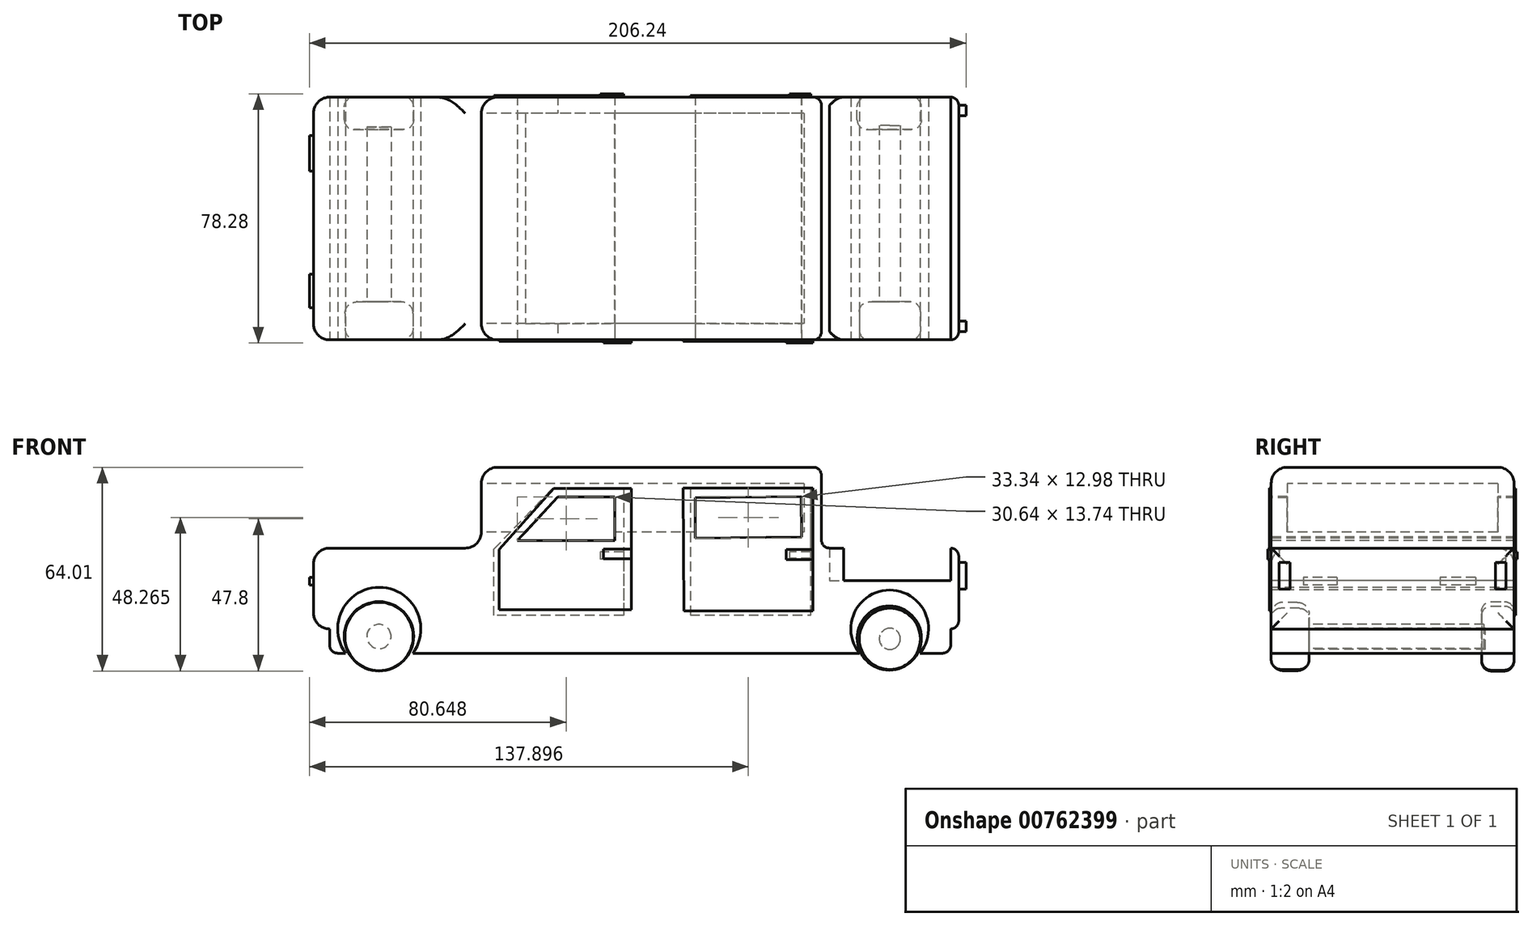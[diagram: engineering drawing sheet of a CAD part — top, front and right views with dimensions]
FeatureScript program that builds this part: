
annotation { "Feature Type Name" : "Feature", "Feature Type Description" : "" }
export const myFeature = defineFeature(function(context is Context, id is Id, definition is map)
    precondition{}
    {
        {
            var Q0;
            Q0=qCreatedBy(makeId("Top.planeOp"),FACE);
            var sketch = newSketch(context, id + "F0", { "sketchPlane" : qUnion([Q0])});
            skLineSegment(sketch, "E0.bottom", {"start": v(-103.87, 60.83) * mm, "end": v(98.81, 60.83) * mm});
            skLineSegment(sketch, "E0.top", {"start": v(-103.87, -15.43) * mm, "end": v(98.81, -15.43) * mm});
            skLineSegment(sketch, "E0.left", {"start": v(-103.87, 60.83) * mm, "end": v(-103.87, -15.43) * mm});
            skLineSegment(sketch, "E0.right", {"start": v(98.81, 60.83) * mm, "end": v(98.81, -15.43) * mm});
            skSolve(sketch);
        }
        {
            var Q0;
            Q0 = qSketchRegion(id + "F0", true);
            extrude(context, id + "F1", {"entities" : qUnion([Q0]), "depth" : 25.4 * mm, "offsetDistance" : 25.4 * mm});
        }
        {
            var Q0;
            Q0=makeQuery(id+"F1.opExtrude","CAP_FACE",FACE,{"disambiguationData":[OSD([sQuery(id+"F0.wireOp",EDGE,"E0.bottom"),sQuery(id+"F0.wireOp",EDGE,"E0.top"),sQuery(id+"F0.wireOp",EDGE,"E0.left"),sQuery(id+"F0.wireOp",EDGE,"E0.right")])],"isStart":false});
            var sketch = newSketch(context, id + "F2", { "sketchPlane" : qUnion([Q0])});
            skLineSegment(sketch, "E1.bottom", {"start": v(-51.1, 60.83) * mm, "end": v(55.69, 60.83) * mm});
            skLineSegment(sketch, "E1.top", {"start": v(-51.1, -15.43) * mm, "end": v(55.69, -15.43) * mm});
            skLineSegment(sketch, "E1.left", {"start": v(-51.1, 60.83) * mm, "end": v(-51.1, -15.43) * mm});
            skLineSegment(sketch, "E1.right", {"start": v(55.69, 60.83) * mm, "end": v(55.69, -15.43) * mm});
            skSolve(sketch);
        }
        {
            var Q0;
            Q0 = qSketchRegion(id + "F2", true);
            extrude(context, id + "F3", {"entities" : qUnion([Q0]), "operationType" : NewBodyOperationType.ADD, "depth" : 25.4 * mm, "offsetDistance" : 25.4 * mm});
        }
        {
            var Q0;
            Q0=makeQuery(id+"F3.opExtrude","CAP_EDGE",EDGE,{"disambiguationData":[OSD([sQuery(id+"F2.wireOp",EDGE,"E1.left")])],"isStart":false});
            var Q1;
            Q1=makeQuery(id+"F3.opExtrude","SWEPT_FACE",FACE,{"disambiguationData":[OSD([sQuery(id+"F2.wireOp",EDGE,"E1.left")])]});
            var Q2;
            Q2=makeQuery(id+"F1.opExtrude","CAP_EDGE",EDGE,{"disambiguationData":[OSD([sQuery(id+"F0.wireOp",EDGE,"E0.left")])],"isStart":false});
            var Q3;
            Q3=makeQuery(id+"F1.opExtrude","SWEPT_FACE",FACE,{"disambiguationData":[OSD([sQuery(id+"F0.wireOp",EDGE,"E0.left")])]});
            fillet(context, id + "F4", {"entities" : qUnion([Q0, Q1, Q2, Q3]), "radius" : 5.08 * mm, "tangentPropagation" : true, "allowEdgeOverflow" : false});
        }
        {
            var Q0;
            Q0=makeQuery(id+"F3.opExtrude","CAP_EDGE",EDGE,{"disambiguationData":[OSD([sQuery(id+"F2.wireOp",EDGE,"E1.right")])],"isStart":false});
            var Q1;
            Q1=makeQuery(id+"F3.opExtrude","SWEPT_FACE",FACE,{"disambiguationData":[OSD([sQuery(id+"F2.wireOp",EDGE,"E1.right")])]});
            fillet(context, id + "F5", {"entities" : qUnion([Q0, Q1]), "radius" : 2.54 * mm, "tangentPropagation" : true, "allowEdgeOverflow" : false});
        }
        {
            var Q0;
            Q0=makeQuery(id+"F1.opExtrude","SWEPT_EDGE",EDGE,{"disambiguationData":[OSD([sQuery(id+"F0.wireOp",EDGE,"E0.bottom"),sQuery(id+"F0.wireOp",EDGE,"E0.right")])]});
            var Q1;
            Q1=makeQuery(id+"F1.opExtrude","SWEPT_FACE",FACE,{"disambiguationData":[OSD([sQuery(id+"F0.wireOp",EDGE,"E0.right")])]});
            fillet(context, id + "F6", {"entities" : qUnion([Q0, Q1]), "radius" : 2.54 * mm, "tangentPropagation" : true, "allowEdgeOverflow" : false});
        }
        {
            var Q0;
            Q0=makeQuery(id+"F1.opExtrude","CAP_FACE",FACE,{"disambiguationData":[OSD([sQuery(id+"F0.wireOp",EDGE,"E0.bottom"),sQuery(id+"F0.wireOp",EDGE,"E0.top"),sQuery(id+"F0.wireOp",EDGE,"E0.left"),sQuery(id+"F0.wireOp",EDGE,"E0.right")])],"isStart":true});
            var sketch = newSketch(context, id + "F7", { "sketchPlane" : qUnion([Q0])});
            skLineSegment(sketch, "E2.bottom", {"start": v(-98.79, 15.43) * mm, "end": v(96.27, 15.43) * mm});
            skLineSegment(sketch, "E2.top", {"start": v(-98.79, -60.83) * mm, "end": v(96.27, -60.83) * mm});
            skLineSegment(sketch, "E2.left", {"start": v(-98.79, 15.43) * mm, "end": v(-98.79, -60.83) * mm});
            skLineSegment(sketch, "E2.right", {"start": v(96.27, 15.43) * mm, "end": v(96.27, -60.83) * mm});
            skSolve(sketch);
        }
        {
            var Q0;
            Q0 = qSketchRegion(id + "F7", true);
            extrude(context, id + "F8", {"entities" : qUnion([Q0]), "operationType" : NewBodyOperationType.ADD, "depth" : 7.62 * mm, "offsetDistance" : 25.4 * mm});
        }
        {
            var Q0;
            Q0=makeQuery(id+"F8.opExtrude","CAP_EDGE",EDGE,{"disambiguationData":[OSD([sQuery(id+"F7.wireOp",EDGE,"E2.left")])],"isStart":false});
            var Q1;
            {var subQ0=sQuery(id+"F0.wireOp",EDGE,"E0.left");Q1=makeQuery(id+"F4.opFillet","BLEND_EDGE",EDGE,{"blendedFrom":[makeQuery(id+"F1.opExtrude","CAP_EDGE",EDGE,{"disambiguationData":[OSD([subQ0])],"isStart":true}),makeQuery(id+"F1.opExtrude","SWEPT_FACE",FACE,{"disambiguationData":[OSD([subQ0])]})],"blendedInto":[makeQuery(id+"F1.opExtrude","SWEPT_FACE",FACE,{"disambiguationData":[OSD([subQ0])]})]});}
            var Q2;
            Q2=makeQuery(id+"F8.opExtrude","CAP_EDGE",EDGE,{"disambiguationData":[OSD([sQuery(id+"F7.wireOp",EDGE,"E2.right")])],"isStart":false});
            fillet(context, id + "F9", {"entities" : qUnion([Q0, Q1, Q2]), "radius" : 2.54 * mm, "tangentPropagation" : true, "allowEdgeOverflow" : false});
        }
        {
            var Q0;
            Q0=makeQuery(id+"F8.boolean.opBoolean","MERGE",FACE,{"derivedFrom":[makeQuery(id+"F3.boolean.opBoolean","MERGE",FACE,{"derivedFrom":[makeQuery(id+"F1.opExtrude","SWEPT_FACE",FACE,{"disambiguationData":[OSD([sQuery(id+"F0.wireOp",EDGE,"E0.bottom")])]}),makeQuery(id+"F3.opExtrude","SWEPT_FACE",FACE,{"disambiguationData":[OSD([sQuery(id+"F2.wireOp",EDGE,"E1.bottom")])]})]}),makeQuery(id+"F8.opExtrude","SWEPT_FACE",FACE,{"disambiguationData":[OSD([sQuery(id+"F7.wireOp",EDGE,"E2.top")])]})]});
            var sketch = newSketch(context, id + "F10", { "sketchPlane" : qUnion([Q0])});
            skLineSegment(sketch, "E3", {"start": v(-54.63, 24.35) * mm, "end": v(48.07, 24.35) * mm});
            skSolve(sketch);
        }
        {
            var Q0;
            Q0=makeQuery(id+"F3.opExtrude","CAP_EDGE",EDGE,{"disambiguationData":[OSD([sQuery(id+"F2.wireOp",EDGE,"E1.bottom")])],"isStart":false});
            var Q1;
            Q1=makeQuery(id+"F3.opExtrude","CAP_EDGE",EDGE,{"disambiguationData":[OSD([sQuery(id+"F2.wireOp",EDGE,"E1.top")])],"isStart":false});
            fillet(context, id + "F11", {"entities" : qUnion([Q0, Q1]), "radius" : 5.08 * mm, "tangentPropagation" : true, "allowEdgeOverflow" : false});
        }
        {
            var Q0;
            Q0=makeQuery(id+"F8.boolean.opBoolean","MERGE",FACE,{"derivedFrom":[makeQuery(id+"F3.boolean.opBoolean","MERGE",FACE,{"derivedFrom":[makeQuery(id+"F1.opExtrude","SWEPT_FACE",FACE,{"disambiguationData":[OSD([sQuery(id+"F0.wireOp",EDGE,"E0.top")])]}),makeQuery(id+"F3.opExtrude","SWEPT_FACE",FACE,{"disambiguationData":[OSD([sQuery(id+"F2.wireOp",EDGE,"E1.top")])]})]}),makeQuery(id+"F8.opExtrude","SWEPT_FACE",FACE,{"disambiguationData":[OSD([sQuery(id+"F7.wireOp",EDGE,"E2.bottom")])]})]});
            var sketch = newSketch(context, id + "F12", { "sketchPlane" : qUnion([Q0])});
            skLineSegment(sketch, "E4", {"start": v(-47.73, 24.83) * mm, "end": v(53.15, 24.83) * mm});
            skLineSegment(sketch, "E5", {"start": v(53.15, 24.83) * mm, "end": v(29.7, 24.83) * mm});
            skLineSegment(sketch, "E6", {"start": v(29.7, 24.83) * mm, "end": v(29.7, 45.72) * mm});
            skSolve(sketch);
        }
        {
            var Q0;
            {var subQ15=sQuery(id+"F12.wireOp",EDGE,"E4");Q0=makeQuery(id+"F12.imprint","IMPRINT",FACE,{"disambiguationData":[TD([[makeQuery(id+"F12.imprint","IMPRINT",EDGE,{"derivedFrom":subQ15}),-1.0]])]});}
            var sketch = newSketch(context, id + "F13", { "sketchPlane" : qUnion([Q0])});
            skCircle(sketch, "E7", {"center": v(-83.66, 0) * mm, "radius": 11.07 * mm});
            skCircle(sketch, "E8", {"center": v(76.6, 0) * mm, "radius": 11.02 * mm});
            skSolve(sketch);
        }
        {
            var Q0;
            Q0=makeQuery(id+"F1.opExtrude","SWEPT_FACE",FACE,{"disambiguationData":[OSD([sQuery(id+"F0.wireOp",EDGE,"E0.left")])]});
            var sketch = newSketch(context, id + "F14", { "sketchPlane" : qUnion([Q0])});
            skSolve(sketch);
        }
        {
            var Q0;
            {var subQ0=sQuery(id+"F0.wireOp",EDGE,"E0.top");var subQ1=sQuery(id+"F0.wireOp",EDGE,"E0.right");var subQ2=sQuery(id+"F0.wireOp",EDGE,"E0.bottom");Q0=makeQuery(id+"F3.boolean.opBoolean","SPLIT",FACE,{"disambiguationData":[TD([makeQuery(id+"F1.opExtrude","SWEPT_FACE",FACE,{"disambiguationData":[OSD([subQ1])]})])],"derivedFrom":makeQuery(id+"F1.opExtrude","CAP_FACE",FACE,{"disambiguationData":[OSD([subQ2,subQ0,sQuery(id+"F0.wireOp",EDGE,"E0.left"),subQ1])],"isStart":false})});}
            var sketch = newSketch(context, id + "F15", { "sketchPlane" : qUnion([Q0])});
            skSolve(sketch);
        }
        {
            var Q0;
            Q0 = qSketchRegion(id + "F13", true);
            extrude(context, id + "F16", {"entities" : qUnion([Q0]), "operationType" : NewBodyOperationType.REMOVE, "oppositeDirection" : true, "depth" : 78.74 * mm, "offsetDistance" : 25.4 * mm});
        }
        {
            var Q0;
            {var subQ1=sQuery(id+"F0.wireOp",EDGE,"E0.top");var subQ3=sQuery(id+"F0.wireOp",EDGE,"E0.right");var subQ4=makeQuery(id+"F1.opExtrude","SWEPT_FACE",FACE,{"disambiguationData":[OSD([subQ3])]});var subQ5=sQuery(id+"F0.wireOp",EDGE,"E0.bottom");var subQ8=sQuery(id+"F2.wireOp",EDGE,"E1.right");var subQ10=makeQuery(id+"F1.opExtrude","CAP_FACE",FACE,{"disambiguationData":[OSD([subQ5,subQ1,sQuery(id+"F0.wireOp",EDGE,"E0.left"),subQ3])],"isStart":false});var subQ11=makeQuery(id+"F3.boolean.opBoolean","SPLIT",FACE,{"disambiguationData":[TD([subQ4])],"derivedFrom":subQ10});Q0=makeQuery(id+"F15.imprint","IMPRINT",FACE,{"disambiguationData":[TD([[makeQuery(id+"F15.imprint","IMPRINT",EDGE,{"derivedFrom":makeQuery(id+"F5.opFillet","BLEND_EDGE",EDGE,{"blendedFrom":[makeQuery(id+"F3.opExtrude","CAP_EDGE",EDGE,{"disambiguationData":[OSD([subQ8])],"isStart":true}),subQ11],"blendedInto":[subQ11]})}),1.0]])]});}
            extrude(context, id + "F17", {"entities" : qUnion([Q0]), "operationType" : NewBodyOperationType.REMOVE, "oppositeDirection" : true, "depth" : 10.16 * mm, "offsetDistance" : 25.4 * mm});
        }
        {
            var Q0;
            {var subQ15=sQuery(id+"F12.wireOp",EDGE,"E4");Q0=makeQuery(id+"F12.imprint","IMPRINT",FACE,{"disambiguationData":[TD([[makeQuery(id+"F12.imprint","IMPRINT",EDGE,{"derivedFrom":subQ15}),-1.0]])]});}
            var sketch = newSketch(context, id + "F18", { "sketchPlane" : qUnion([Q0])});
            skLineSegment(sketch, "E9", {"start": v(12.54, 5.62) * mm, "end": v(53.01, 5.62) * mm});
            skLineSegment(sketch, "E10", {"start": v(53.01, 5.62) * mm, "end": v(53.01, 44.28) * mm});
            skLineSegment(sketch, "E11", {"start": v(53.01, 44.28) * mm, "end": v(12.23, 44.28) * mm});
            skLineSegment(sketch, "E12", {"start": v(12.23, 44.28) * mm, "end": v(12.54, 5.62) * mm});
            skLineSegment(sketch, "E13.bottom", {"start": v(53.01, 24.95) * mm, "end": v(46.24, 24.95) * mm});
            skLineSegment(sketch, "E13.top", {"start": v(53.01, 22.79) * mm, "end": v(46.24, 22.79) * mm});
            skLineSegment(sketch, "E13.left", {"start": v(53.01, 24.95) * mm, "end": v(53.01, 22.79) * mm});
            skLineSegment(sketch, "E13.right", {"start": v(46.24, 24.95) * mm, "end": v(46.24, 22.79) * mm});
            skSolve(sketch);
        }
        {
            var Q0;
            Q0 = qSketchRegion(id + "F18", true);
            extrude(context, id + "F19", {"entities" : qUnion([Q0]), "operationType" : NewBodyOperationType.ADD, "depth" : 0.5 * mm, "offsetDistance" : 25.4 * mm});
        }
        {
            var Q0;
            {var subQ7=sQuery(id+"F10.wireOp",EDGE,"E3");Q0=makeQuery(id+"F10.imprint","IMPRINT",FACE,{"disambiguationData":[TD([[makeQuery(id+"F10.imprint","IMPRINT",EDGE,{"derivedFrom":subQ7}),1.0]])]});}
            var sketch = newSketch(context, id + "F20", { "sketchPlane" : qUnion([Q0])});
            skLineSegment(sketch, "E14", {"start": v(47.15, 25.07) * mm, "end": v(28.86, 44.1) * mm});
            skLineSegment(sketch, "E15", {"start": v(28.86, 44.1) * mm, "end": v(6.43, 44.1) * mm});
            skLineSegment(sketch, "E16", {"start": v(6.43, 44.1) * mm, "end": v(6.43, 4.2) * mm});
            skLineSegment(sketch, "E17", {"start": v(6.43, 4.2) * mm, "end": v(47.15, 4.2) * mm});
            skLineSegment(sketch, "E18", {"start": v(47.15, 4.2) * mm, "end": v(47.15, 25.07) * mm});
            skLineSegment(sketch, "E19", {"start": v(-14.5, 44.1) * mm, "end": v(-14.5, 4.4) * mm});
            skLineSegment(sketch, "E20", {"start": v(-14.5, 4.4) * mm, "end": v(-52.38, 4.4) * mm});
            skLineSegment(sketch, "E21", {"start": v(-52.38, 4.4) * mm, "end": v(-52.38, 44.1) * mm});
            skLineSegment(sketch, "E22", {"start": v(-52.38, 44.1) * mm, "end": v(-14.5, 44.1) * mm});
            skLineSegment(sketch, "E23.bottom", {"start": v(-52.38, 24.24) * mm, "end": v(-46.53, 24.24) * mm});
            skLineSegment(sketch, "E23.top", {"start": v(-52.38, 26.16) * mm, "end": v(-46.53, 26.16) * mm});
            skLineSegment(sketch, "E23.left", {"start": v(-52.38, 24.24) * mm, "end": v(-52.38, 26.16) * mm});
            skLineSegment(sketch, "E23.right", {"start": v(-46.53, 24.24) * mm, "end": v(-46.53, 26.16) * mm});
            skLineSegment(sketch, "E24.bottom", {"start": v(6.43, 24.15) * mm, "end": v(15.68, 24.15) * mm});
            skLineSegment(sketch, "E24.top", {"start": v(6.43, 26.16) * mm, "end": v(15.68, 26.16) * mm});
            skLineSegment(sketch, "E24.left", {"start": v(6.43, 24.15) * mm, "end": v(6.43, 26.16) * mm});
            skLineSegment(sketch, "E24.right", {"start": v(15.68, 24.15) * mm, "end": v(15.68, 26.16) * mm});
            skSolve(sketch);
        }
        {
            var Q0;
            Q0 = qSketchRegion(id + "F20", true);
            extrude(context, id + "F21", {"entities" : qUnion([Q0]), "operationType" : NewBodyOperationType.ADD, "depth" : 0.5 * mm, "offsetDistance" : 25.4 * mm});
        }
        {
            var Q0;
            Q0=makeQuery(id+"F21.opExtrude","CAP_FACE",FACE,{"disambiguationData":[OSD([sQuery(id+"F20.wireOp",EDGE,"E14"),sQuery(id+"F20.wireOp",EDGE,"E15"),sQuery(id+"F20.wireOp",EDGE,"E16"),sQuery(id+"F20.wireOp",EDGE,"E17"),sQuery(id+"F20.wireOp",EDGE,"E18"),sQuery(id+"F20.wireOp",EDGE,"E24.left")])],"isStart":false});
            var sketch = newSketch(context, id + "F22", { "sketchPlane" : qUnion([Q0])});
            skLineSegment(sketch, "E25.bottom", {"start": v(6.43, 24.15) * mm, "end": v(13.75, 24.15) * mm});
            skLineSegment(sketch, "E25.top", {"start": v(6.43, 21.96) * mm, "end": v(13.75, 21.96) * mm});
            skLineSegment(sketch, "E25.left", {"start": v(6.43, 24.15) * mm, "end": v(6.43, 21.96) * mm});
            skLineSegment(sketch, "E25.right", {"start": v(13.75, 24.15) * mm, "end": v(13.75, 21.96) * mm});
            skSolve(sketch);
        }
        {
            var Q0;
            Q0 = qSketchRegion(id + "F22", true);
            extrude(context, id + "F23", {"entities" : qUnion([Q0]), "operationType" : NewBodyOperationType.ADD, "depth" : 0.5 * mm, "offsetDistance" : 25.4 * mm});
        }
        {
            var Q0;
            Q0=makeQuery(id+"F21.opExtrude","CAP_FACE",FACE,{"disambiguationData":[OSD([sQuery(id+"F20.wireOp",EDGE,"E19"),sQuery(id+"F20.wireOp",EDGE,"E20"),sQuery(id+"F20.wireOp",EDGE,"E21"),sQuery(id+"F20.wireOp",EDGE,"E22"),sQuery(id+"F20.wireOp",EDGE,"E23.left")])],"isStart":false});
            var sketch = newSketch(context, id + "F24", { "sketchPlane" : qUnion([Q0])});
            skLineSegment(sketch, "E26.bottom", {"start": v(-52.38, 24.24) * mm, "end": v(-45.61, 24.24) * mm});
            skLineSegment(sketch, "E26.top", {"start": v(-52.38, 22.14) * mm, "end": v(-45.61, 22.14) * mm});
            skLineSegment(sketch, "E26.left", {"start": v(-52.38, 24.24) * mm, "end": v(-52.38, 22.14) * mm});
            skLineSegment(sketch, "E26.right", {"start": v(-45.61, 24.24) * mm, "end": v(-45.61, 22.14) * mm});
            skSolve(sketch);
        }
        {
            var Q0;
            Q0 = qSketchRegion(id + "F24", true);
            extrude(context, id + "F25", {"entities" : qUnion([Q0]), "operationType" : NewBodyOperationType.ADD, "depth" : 0.5 * mm, "offsetDistance" : 25.4 * mm});
        }
        {
            var Q0;
            {var subQ6=sQuery(id+"F12.wireOp",EDGE,"E4");Q0=makeQuery(id+"F12.imprint","IMPRINT",FACE,{"disambiguationData":[TD([[makeQuery(id+"F12.imprint","IMPRINT",EDGE,{"derivedFrom":subQ6}),1.0]])]});}
            var sketch = newSketch(context, id + "F26", { "sketchPlane" : qUnion([Q0])});
            skLineSegment(sketch, "E27", {"start": v(-45.52, 24.97) * mm, "end": v(-45.52, 6.03) * mm});
            skLineSegment(sketch, "E28", {"start": v(-45.52, 6.03) * mm, "end": v(-4.02, 6.03) * mm});
            skLineSegment(sketch, "E29", {"start": v(-4.02, 6.03) * mm, "end": v(-4.02, 44.14) * mm});
            skLineSegment(sketch, "E30", {"start": v(-4.02, 44.14) * mm, "end": v(-28.38, 44.14) * mm});
            skLineSegment(sketch, "E31", {"start": v(-28.38, 44.14) * mm, "end": v(-45.52, 24.97) * mm});
            skSolve(sketch);
        }
        {
            var Q0;
            Q0 = qSketchRegion(id + "F26", true);
            extrude(context, id + "F27", {"entities" : qUnion([Q0]), "operationType" : NewBodyOperationType.ADD, "depth" : 0.5 * mm, "offsetDistance" : 25.4 * mm});
        }
        {
            var Q0;
            Q0=makeQuery(id+"F27.opExtrude","CAP_FACE",FACE,{"disambiguationData":[OSD([sQuery(id+"F26.wireOp",EDGE,"E27"),sQuery(id+"F26.wireOp",EDGE,"E28"),sQuery(id+"F26.wireOp",EDGE,"E29"),sQuery(id+"F26.wireOp",EDGE,"E30"),sQuery(id+"F26.wireOp",EDGE,"E31")])],"isStart":false});
            var sketch = newSketch(context, id + "F28", { "sketchPlane" : qUnion([Q0])});
            skLineSegment(sketch, "E32.bottom", {"start": v(-4.02, 25.09) * mm, "end": v(-12.82, 25.09) * mm});
            skLineSegment(sketch, "E32.top", {"start": v(-4.02, 22.04) * mm, "end": v(-12.82, 22.04) * mm});
            skLineSegment(sketch, "E32.left", {"start": v(-4.02, 25.09) * mm, "end": v(-4.02, 22.04) * mm});
            skLineSegment(sketch, "E32.right", {"start": v(-12.82, 25.09) * mm, "end": v(-12.82, 22.04) * mm});
            skSolve(sketch);
        }
        {
            var Q0;
            Q0 = qSketchRegion(id + "F28", true);
            extrude(context, id + "F29", {"entities" : qUnion([Q0]), "operationType" : NewBodyOperationType.ADD, "depth" : 0.5 * mm, "offsetDistance" : 25.4 * mm});
        }
        {
            var Q0;
            Q0=makeQuery(id+"F19.opExtrude","CAP_FACE",FACE,{"disambiguationData":[OSD([sQuery(id+"F18.wireOp",EDGE,"E9"),sQuery(id+"F18.wireOp",EDGE,"E10"),sQuery(id+"F18.wireOp",EDGE,"E11"),sQuery(id+"F18.wireOp",EDGE,"E12"),sQuery(id+"F18.wireOp",EDGE,"E13.left")])],"isStart":false});
            var sketch = newSketch(context, id + "F30", { "sketchPlane" : qUnion([Q0])});
            skLineSegment(sketch, "E33.bottom", {"start": v(53.01, 24.95) * mm, "end": v(44.7, 24.95) * mm});
            skLineSegment(sketch, "E33.top", {"start": v(53.01, 21.82) * mm, "end": v(44.7, 21.82) * mm});
            skLineSegment(sketch, "E33.left", {"start": v(53.01, 24.95) * mm, "end": v(53.01, 21.82) * mm});
            skLineSegment(sketch, "E33.right", {"start": v(44.7, 24.95) * mm, "end": v(44.7, 21.82) * mm});
            skSolve(sketch);
        }
        {
            var Q0;
            Q0 = qSketchRegion(id + "F30", true);
            extrude(context, id + "F31", {"entities" : qUnion([Q0]), "operationType" : NewBodyOperationType.ADD, "depth" : 0.5 * mm, "offsetDistance" : 25.4 * mm});
        }
        {
            var Q0;
            Q0=makeQuery(id+"F27.opExtrude","CAP_FACE",FACE,{"disambiguationData":[OSD([sQuery(id+"F26.wireOp",EDGE,"E27"),sQuery(id+"F26.wireOp",EDGE,"E28"),sQuery(id+"F26.wireOp",EDGE,"E29"),sQuery(id+"F26.wireOp",EDGE,"E30"),sQuery(id+"F26.wireOp",EDGE,"E31")])],"isStart":false});
            var sketch = newSketch(context, id + "F32", { "sketchPlane" : qUnion([Q0])});
            skLineSegment(sketch, "E34", {"start": v(-39.66, 27.45) * mm, "end": v(-27.24, 41.33) * mm});
            skLineSegment(sketch, "E35", {"start": v(-27.24, 41.33) * mm, "end": v(-9.2, 41.33) * mm});
            skLineSegment(sketch, "E36", {"start": v(-9.2, 41.33) * mm, "end": v(-9.2, 27.45) * mm});
            skLineSegment(sketch, "E37", {"start": v(-9.2, 27.45) * mm, "end": v(-39.66, 27.45) * mm});
            skSolve(sketch);
        }
        {
            var Q0;
            Q0=makeQuery(id+"F3.opExtrude","SWEPT_FACE",FACE,{"disambiguationData":[OSD([sQuery(id+"F2.wireOp",EDGE,"E1.left")])]});
            extrude(context, id + "F33", {"entities" : qUnion([Q0]), "operationType" : NewBodyOperationType.REMOVE, "oppositeDirection" : true, "depth" : 101.35 * mm, "offsetDistance" : 25.4 * mm});
        }
        {
            var Q0;
            Q0=makeQuery(id+"F1.opExtrude","SWEPT_FACE",FACE,{"disambiguationData":[OSD([sQuery(id+"F0.wireOp",EDGE,"E0.right")])]});
            var sketch = newSketch(context, id + "F34", { "sketchPlane" : qUnion([Q0])});
            skLineSegment(sketch, "E38.bottom", {"start": v(-12.89, 20.9) * mm, "end": v(-9.54, 20.9) * mm});
            skLineSegment(sketch, "E38.top", {"start": v(-12.89, 12.53) * mm, "end": v(-9.54, 12.53) * mm});
            skLineSegment(sketch, "E38.left", {"start": v(-12.89, 20.9) * mm, "end": v(-12.89, 12.53) * mm});
            skLineSegment(sketch, "E38.right", {"start": v(-9.54, 20.9) * mm, "end": v(-9.54, 12.53) * mm});
            skLineSegment(sketch, "E39.bottom", {"start": v(58.29, 20.9) * mm, "end": v(54.96, 20.9) * mm});
            skLineSegment(sketch, "E39.top", {"start": v(58.29, 12.53) * mm, "end": v(54.96, 12.53) * mm});
            skLineSegment(sketch, "E39.left", {"start": v(58.29, 20.9) * mm, "end": v(58.29, 12.53) * mm});
            skLineSegment(sketch, "E39.right", {"start": v(54.96, 20.9) * mm, "end": v(54.96, 12.53) * mm});
            skSolve(sketch);
        }
        {
            var Q0;
            Q0 = qSketchRegion(id + "F34", true);
            extrude(context, id + "F35", {"entities" : qUnion([Q0]), "operationType" : NewBodyOperationType.ADD, "depth" : 2.3 * mm, "offsetDistance" : 25.4 * mm});
        }
        {
            var Q0;
            {var subQ0=sQuery(id+"F0.wireOp",EDGE,"E0.left");var subQ1=makeQuery(id+"F1.opExtrude","SWEPT_FACE",FACE,{"disambiguationData":[OSD([subQ0])]});Q0=makeQuery(id+"F14.imprint","IMPRINT",FACE,{"disambiguationData":[TD([[makeQuery(id+"F14.imprint","IMPRINT",EDGE,{"derivedFrom":makeQuery(id+"F4.opFillet","BLEND_EDGE",EDGE,{"blendedFrom":[makeQuery(id+"F1.opExtrude","CAP_EDGE",EDGE,{"disambiguationData":[OSD([subQ0])],"isStart":true}),subQ1],"blendedInto":[subQ1]})}),1.0]])]});}
            var sketch = newSketch(context, id + "F36", { "sketchPlane" : qUnion([Q0])});
            skLineSegment(sketch, "E40.bottom", {"start": v(-48.8, 16.23) * mm, "end": v(-37.64, 16.23) * mm});
            skLineSegment(sketch, "E40.top", {"start": v(-48.8, 13.78) * mm, "end": v(-37.64, 13.78) * mm});
            skLineSegment(sketch, "E40.left", {"start": v(-48.8, 16.23) * mm, "end": v(-48.8, 13.78) * mm});
            skLineSegment(sketch, "E40.right", {"start": v(-37.64, 16.23) * mm, "end": v(-37.64, 13.78) * mm});
            skLineSegment(sketch, "E41.bottom", {"start": v(-5.26, 16.23) * mm, "end": v(5.35, 16.23) * mm});
            skLineSegment(sketch, "E41.top", {"start": v(-5.26, 13.78) * mm, "end": v(5.35, 13.78) * mm});
            skLineSegment(sketch, "E41.left", {"start": v(-5.26, 16.23) * mm, "end": v(-5.26, 13.78) * mm});
            skLineSegment(sketch, "E41.right", {"start": v(5.35, 16.23) * mm, "end": v(5.35, 13.78) * mm});
            skSolve(sketch);
        }
        {
            var Q0;
            Q0 = qSketchRegion(id + "F36", true);
            extrude(context, id + "F37", {"entities" : qUnion([Q0]), "operationType" : NewBodyOperationType.ADD, "depth" : 1.27 * mm, "offsetDistance" : 25.4 * mm});
        }
        {
            var Q0;
            Q0 = qSketchRegion(id + "F20", true);
            extrude(context, id + "F38", {"entities" : qUnion([Q0]), "operationType" : NewBodyOperationType.ADD, "depth" : 0.5 * mm, "offsetDistance" : 25.4 * mm});
        }
        {
            var Q0;
            Q0=makeQuery(id+"F32.imprint","IMPRINT",FACE,{"disambiguationData":[TD([[makeQuery(id+"F32.imprint","IMPRINT",EDGE,{"derivedFrom":sQuery(id+"F32.wireOp",EDGE,"E34")}),1.0]])]});
            var sketch = newSketch(context, id + "F39", { "sketchPlane" : qUnion([Q0])});
            skLineSegment(sketch, "E42", {"start": v(-39.81, 27.72) * mm, "end": v(-27.19, 41.46) * mm});
            skLineSegment(sketch, "E43", {"start": v(-27.19, 41.46) * mm, "end": v(-9.17, 41.46) * mm});
            skLineSegment(sketch, "E44", {"start": v(-9.17, 41.46) * mm, "end": v(-9.17, 27.72) * mm});
            skLineSegment(sketch, "E45", {"start": v(-9.17, 27.72) * mm, "end": v(-39.81, 27.72) * mm});
            skSolve(sketch);
        }
        {
            var Q0;
            Q0 = qSketchRegion(id + "F39", true);
            extrude(context, id + "F40", {"entities" : qUnion([Q0]), "operationType" : NewBodyOperationType.REMOVE, "oppositeDirection" : true, "depth" : 85.85 * mm, "offsetDistance" : 25.4 * mm});
        }
        {
            var Q0;
            Q0=makeQuery(id+"F19.opExtrude","CAP_FACE",FACE,{"disambiguationData":[OSD([sQuery(id+"F18.wireOp",EDGE,"E9"),sQuery(id+"F18.wireOp",EDGE,"E10"),sQuery(id+"F18.wireOp",EDGE,"E11"),sQuery(id+"F18.wireOp",EDGE,"E12"),sQuery(id+"F18.wireOp",EDGE,"E13.left")])],"isStart":false});
            var sketch = newSketch(context, id + "F41", { "sketchPlane" : qUnion([Q0])});
            skLineSegment(sketch, "E46", {"start": v(16.09, 41.28) * mm, "end": v(49.32, 41.55) * mm});
            skLineSegment(sketch, "E47", {"start": v(49.32, 41.55) * mm, "end": v(49.42, 28.83) * mm});
            skLineSegment(sketch, "E48", {"start": v(49.42, 28.83) * mm, "end": v(16.09, 28.56) * mm});
            skLineSegment(sketch, "E49", {"start": v(16.09, 28.56) * mm, "end": v(16.09, 41.28) * mm});
            skSolve(sketch);
        }
        {
            var Q0;
            Q0 = qSketchRegion(id + "F41", true);
            extrude(context, id + "F42", {"entities" : qUnion([Q0]), "operationType" : NewBodyOperationType.REMOVE, "oppositeDirection" : true, "depth" : 88.14 * mm, "offsetDistance" : 25.4 * mm});
        }
        {
            var Q0;
            {var subQ15=sQuery(id+"F12.wireOp",EDGE,"E4");Q0=makeQuery(id+"F12.imprint","IMPRINT",FACE,{"disambiguationData":[TD([[makeQuery(id+"F12.imprint","IMPRINT",EDGE,{"derivedFrom":subQ15}),-1.0]])]});}
            var sketch = newSketch(context, id + "F43", { "sketchPlane" : qUnion([Q0])});
            skCircle(sketch, "E50", {"center": v(-83.2, 0) * mm, "radius": 13.06 * mm});
            skCircle(sketch, "E51", {"center": v(77.13, 0) * mm, "radius": 12.2 * mm});
            skSolve(sketch);
        }
        {
            var Q0;
            Q0 = qSketchRegion(id + "F43", true);
            extrude(context, id + "F44", {"entities" : qUnion([Q0]), "operationType" : NewBodyOperationType.REMOVE, "oppositeDirection" : true, "depth" : 84.33 * mm, "offsetDistance" : 25.4 * mm});
        }
        {
            var Q0;
            {var subQ15=sQuery(id+"F12.wireOp",EDGE,"E4");Q0=makeQuery(id+"F12.imprint","IMPRINT",FACE,{"disambiguationData":[TD([[makeQuery(id+"F12.imprint","IMPRINT",EDGE,{"derivedFrom":subQ15}),-1.0]])]});}
            var sketch = newSketch(context, id + "F45", { "sketchPlane" : qUnion([Q0])});
            skCircle(sketch, "E52", {"center": v(-83.27, -2.37) * mm, "radius": 10.72 * mm});
            skCircle(sketch, "E53", {"center": v(77.19, -3.11) * mm, "radius": 9.6 * mm});
            skSolve(sketch);
        }
        {
            var Q0;
            Q0 = qSketchRegion(id + "F45", true);
            extrude(context, id + "F46", {"entities" : qUnion([Q0]), "oppositeDirection" : true, "depth" : 11.94 * mm, "offsetDistance" : 25.4 * mm});
        }
        {
            var Q0;
            Q0=makeQuery(id+"F46.opExtrude","CAP_FACE",FACE,{"disambiguationData":[OSD([sQuery(id+"F45.wireOp",EDGE,"E52")])],"isStart":false});
            var Q1;
            Q1=makeQuery(id+"F46.opExtrude","CAP_EDGE",EDGE,{"disambiguationData":[OSD([sQuery(id+"F45.wireOp",EDGE,"E52")])],"isStart":true});
            fillet(context, id + "F47", {"entities" : qUnion([Q0, Q1]), "radius" : 3.68 * mm, "tangentPropagation" : true, "allowEdgeOverflow" : false});
        }
        {
            var Q0;
            Q0=makeQuery(id+"F46.opExtrude","CAP_EDGE",EDGE,{"disambiguationData":[OSD([sQuery(id+"F45.wireOp",EDGE,"E53")])],"isStart":false});
            var Q1;
            Q1=makeQuery(id+"F46.opExtrude","CAP_EDGE",EDGE,{"disambiguationData":[OSD([sQuery(id+"F45.wireOp",EDGE,"E53")])],"isStart":true});
            fillet(context, id + "F48", {"entities" : qUnion([Q0, Q1]), "radius" : 3.07 * mm, "tangentPropagation" : true, "allowEdgeOverflow" : false});
        }
        {
            var Q0;
            Q0=makeQuery(id+"F46.opExtrude","CAP_FACE",FACE,{"disambiguationData":[OSD([sQuery(id+"F45.wireOp",EDGE,"E53")])],"isStart":false});
            var sketch = newSketch(context, id + "F49", { "sketchPlane" : qUnion([Q0])});
            skCircle(sketch, "E54", {"center": v(-77.19, -3.11) * mm, "radius": 3.3 * mm});
            skSolve(sketch);
        }
        {
            var Q0;
            Q0 = qSketchRegion(id + "F49", true);
            extrude(context, id + "F50", {"entities" : qUnion([Q0]), "operationType" : NewBodyOperationType.ADD, "depth" : 55.37 * mm, "offsetDistance" : 25.4 * mm});
        }
        {
            var Q0;
            {var subQ17=sQuery(id+"F10.wireOp",EDGE,"E3");Q0=makeQuery(id+"F10.imprint","IMPRINT",FACE,{"disambiguationData":[TD([[makeQuery(id+"F10.imprint","IMPRINT",EDGE,{"derivedFrom":subQ17}),-1.0]])]});}
            var sketch = newSketch(context, id + "F51", { "sketchPlane" : qUnion([Q0])});
            skCircle(sketch, "E55", {"center": v(-77, -2.87) * mm, "radius": 10.1 * mm});
            skCircle(sketch, "E56", {"center": v(83.27, -2.31) * mm, "radius": 10.9 * mm});
            skSolve(sketch);
        }
        {
            var Q0;
            Q0 = qSketchRegion(id + "F51", true);
            extrude(context, id + "F52", {"entities" : qUnion([Q0]), "oppositeDirection" : true, "depth" : 10.16 * mm, "offsetDistance" : 25.4 * mm});
        }
        {
            var Q0;
            Q0=makeQuery(id+"F52.opExtrude","CAP_EDGE",EDGE,{"disambiguationData":[OSD([sQuery(id+"F51.wireOp",EDGE,"E55")])],"isStart":true});
            var Q1;
            Q1=makeQuery(id+"F52.opExtrude","CAP_EDGE",EDGE,{"disambiguationData":[OSD([sQuery(id+"F51.wireOp",EDGE,"E55")])],"isStart":false});
            fillet(context, id + "F53", {"entities" : qUnion([Q0, Q1]), "radius" : 3.07 * mm, "tangentPropagation" : true, "allowEdgeOverflow" : false});
        }
        {
            var Q0;
            Q0=makeQuery(id+"F52.opExtrude","CAP_EDGE",EDGE,{"disambiguationData":[OSD([sQuery(id+"F51.wireOp",EDGE,"E56")])],"isStart":true});
            var Q1;
            Q1=makeQuery(id+"F52.opExtrude","CAP_EDGE",EDGE,{"disambiguationData":[OSD([sQuery(id+"F51.wireOp",EDGE,"E56")])],"isStart":false});
            fillet(context, id + "F54", {"entities" : qUnion([Q0, Q1]), "radius" : 3.07 * mm, "tangentPropagation" : true, "allowEdgeOverflow" : false});
        }
        {
            var Q0;
            Q0=makeQuery(id+"F46.opExtrude","CAP_FACE",FACE,{"disambiguationData":[OSD([sQuery(id+"F45.wireOp",EDGE,"E52")])],"isStart":false});
            var sketch = newSketch(context, id + "F55", { "sketchPlane" : qUnion([Q0])});
            skCircle(sketch, "E57", {"center": v(83.27, -2.37) * mm, "radius": 3.8 * mm});
            skSolve(sketch);
        }
        {
            var Q0;
            Q0 = qSketchRegion(id + "F55", true);
            extrude(context, id + "F56", {"entities" : qUnion([Q0]), "depth" : 54.86 * mm, "offsetDistance" : 25.4 * mm});
        }
    });
